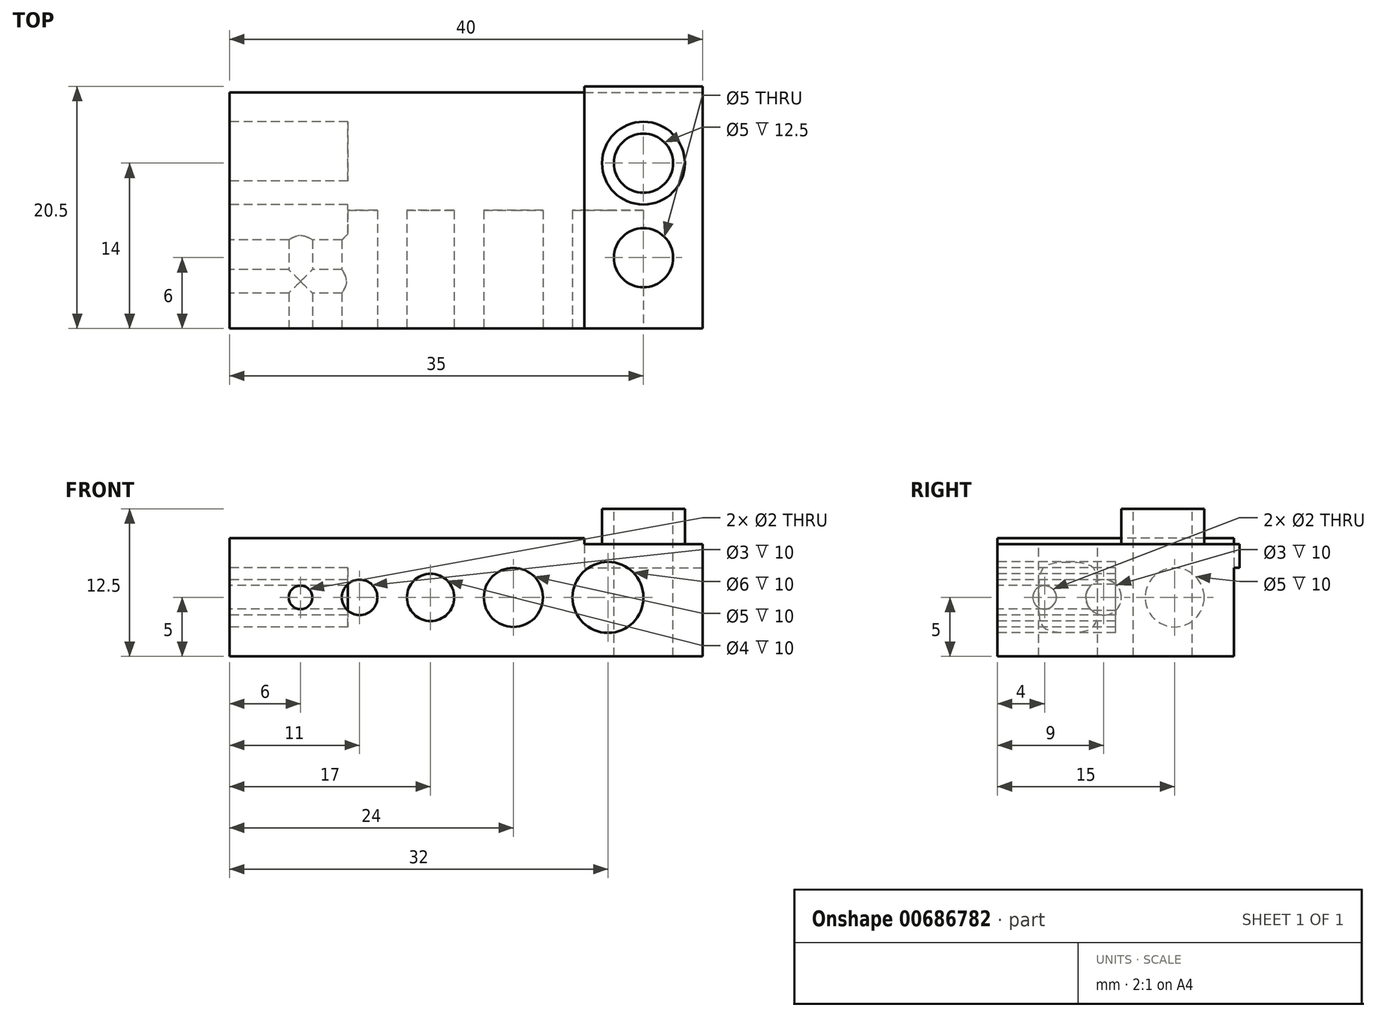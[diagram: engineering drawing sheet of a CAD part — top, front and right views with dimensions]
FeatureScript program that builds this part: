
annotation { "Feature Type Name" : "Feature", "Feature Type Description" : "" }
export const myFeature = defineFeature(function(context is Context, id is Id, definition is map)
    precondition{}
    {
        {
            var Q0;
            Q0=qCreatedBy(makeId("Top.planeOp"),FACE);
            var sketch = newSketch(context, id + "F0", { "sketchPlane" : qUnion([Q0])});
            skLineSegment(sketch, "E0.bottom", {"start": v(-20, 10) * mm, "end": v(20, 10) * mm});
            skLineSegment(sketch, "E0.top", {"start": v(-20, -10) * mm, "end": v(20, -10) * mm});
            skLineSegment(sketch, "E0.left", {"start": v(-20, 10) * mm, "end": v(-20, -10) * mm});
            skLineSegment(sketch, "E0.right", {"start": v(20, 10) * mm, "end": v(20, -10) * mm});
            skPoint(sketch, "E0.middle", {"position": v(0, 0) * mm});
            skSolve(sketch);
        }
        {
            var Q0;
            Q0=makeQuery(id+"F0.imprint","IMPRINT",FACE,{"disambiguationData":[TD([[makeQuery(id+"F0.imprint","IMPRINT",EDGE,{"derivedFrom":sQuery(id+"F0.wireOp",EDGE,"E0.bottom")}),-1.0]])]});
            extrude(context, id + "F1", {"entities" : qUnion([Q0]), "depth" : 10 * mm, "offsetDistance" : 25 * mm});
        }
        {
            var Q0;
            Q0=makeQuery(id+"F1.opExtrude","SWEPT_FACE",FACE,{"disambiguationData":[OSD([sQuery(id+"F0.wireOp",EDGE,"E0.left")])]});
            var sketch = newSketch(context, id + "F2", { "sketchPlane" : qUnion([Q0])});
            skCircle(sketch, "E1", {"center": v(6, 5) * mm, "radius": 1 * mm});
            skCircle(sketch, "E2", {"center": v(-5, 5) * mm, "radius": 2.5 * mm});
            skCircle(sketch, "E3", {"center": v(1, 5) * mm, "radius": 1.5 * mm});
            skSolve(sketch);
        }
        {
            var Q0;
            Q0 = qSketchRegion(id + "F2", true);
            extrude(context, id + "F3", {"entities" : qUnion([Q0]), "operationType" : NewBodyOperationType.REMOVE, "oppositeDirection" : true, "depth" : 10 * mm, "offsetDistance" : 25 * mm});
        }
        {
            var Q0;
            Q0=makeQuery(id+"F1.opExtrude","SWEPT_FACE",FACE,{"disambiguationData":[OSD([sQuery(id+"F0.wireOp",EDGE,"E0.top")])]});
            var sketch = newSketch(context, id + "F4", { "sketchPlane" : qUnion([Q0])});
            skCircle(sketch, "E4", {"center": v(-9, 5) * mm, "radius": 1.5 * mm});
            skCircle(sketch, "E5", {"center": v(-3, 5) * mm, "radius": 2 * mm});
            skCircle(sketch, "E6", {"center": v(4, 5) * mm, "radius": 2.5 * mm});
            skCircle(sketch, "E7", {"center": v(12, 5) * mm, "radius": 3 * mm});
            skCircle(sketch, "E8", {"center": v(-14, 5) * mm, "radius": 1 * mm});
            skSolve(sketch);
        }
        {
            var Q0;
            Q0 = qSketchRegion(id + "F4", true);
            extrude(context, id + "F5", {"entities" : qUnion([Q0]), "operationType" : NewBodyOperationType.REMOVE, "oppositeDirection" : true, "depth" : 10 * mm, "offsetDistance" : 25 * mm});
        }
        {
            var Q0;
            Q0=makeQuery(id+"F1.opExtrude","SWEPT_FACE",FACE,{"disambiguationData":[OSD([sQuery(id+"F0.wireOp",EDGE,"E0.top")])]});
            var sketch = newSketch(context, id + "F6", { "sketchPlane" : qUnion([Q0])});
            skLineSegment(sketch, "E9.bottom", {"start": v(20, 10) * mm, "end": v(10, 10) * mm});
            skLineSegment(sketch, "E9.top", {"start": v(20, 9.5) * mm, "end": v(10, 9.5) * mm});
            skLineSegment(sketch, "E9.left", {"start": v(20, 10) * mm, "end": v(20, 9.5) * mm});
            skLineSegment(sketch, "E9.right", {"start": v(10, 10) * mm, "end": v(10, 9.5) * mm});
            skSolve(sketch);
        }
        {
            var Q0;
            Q0 = qSketchRegion(id + "F6", true);
            extrude(context, id + "F7", {"entities" : qUnion([Q0]), "operationType" : NewBodyOperationType.REMOVE, "endBound" : BoundingType.THROUGH_ALL, "oppositeDirection" : true, "depth" : 25 * mm, "offsetDistance" : 25 * mm});
        }
        {
            var Q0;
            Q0=makeQuery(id+"F7.boolean.opBoolean","COPY",FACE,{"derivedFrom":makeQuery(id+"F7.opExtrude","SWEPT_FACE",FACE,{"disambiguationData":[OSD([sQuery(id+"F6.wireOp",EDGE,"E9.top")])]})});
            var sketch = newSketch(context, id + "F8", { "sketchPlane" : qUnion([Q0])});
            skCircle(sketch, "E10", {"center": v(15, 4) * mm, "radius": 2.5 * mm});
            skCircle(sketch, "E11.MirrorC", {"center": v(15, -4) * mm, "radius": 2.5 * mm});
            skSolve(sketch);
        }
        {
            var Q0;
            Q0 = qSketchRegion(id + "F8", true);
            extrude(context, id + "F9", {"entities" : qUnion([Q0]), "operationType" : NewBodyOperationType.REMOVE, "endBound" : BoundingType.THROUGH_ALL, "oppositeDirection" : true, "depth" : 25 * mm, "offsetDistance" : 25 * mm});
        }
        {
            var Q0;
            Q0=makeQuery(id+"F7.boolean.opBoolean","COPY",FACE,{"derivedFrom":makeQuery(id+"F7.opExtrude","SWEPT_FACE",FACE,{"disambiguationData":[OSD([sQuery(id+"F6.wireOp",EDGE,"E9.top")])]})});
            var sketch = newSketch(context, id + "F10", { "sketchPlane" : qUnion([Q0])});
            skCircle(sketch, "E12", {"center": v(15, 4) * mm, "radius": 3.5 * mm});
            skCircle(sketch, "E13", {"center": v(15, 4) * mm, "radius": 2.5 * mm});
            skSolve(sketch);
        }
        {
            var Q0;
            Q0 = qSketchRegion(id + "F10", true);
            extrude(context, id + "F11", {"entities" : qUnion([Q0]), "operationType" : NewBodyOperationType.ADD, "depth" : 3 * mm, "offsetDistance" : 25 * mm});
        }
        {
            var Q0;
            Q0=makeQuery(id+"F1.opExtrude","SWEPT_FACE",FACE,{"disambiguationData":[OSD([sQuery(id+"F0.wireOp",EDGE,"E0.right")])]});
            var sketch = newSketch(context, id + "F12", { "sketchPlane" : qUnion([Q0])});
            skLineSegment(sketch, "E14.bottom", {"start": v(10.5, 9.5) * mm, "end": v(10, 9.5) * mm});
            skLineSegment(sketch, "E14.top", {"start": v(10.5, 7.5) * mm, "end": v(10, 7.5) * mm});
            skLineSegment(sketch, "E14.left", {"start": v(10.5, 9.5) * mm, "end": v(10.5, 7.5) * mm});
            skLineSegment(sketch, "E14.right", {"start": v(10, 9.5) * mm, "end": v(10, 7.5) * mm});
            skSolve(sketch);
        }
        {
            var Q0;
            Q0 = qSketchRegion(id + "F12", true);
            extrude(context, id + "F13", {"entities" : qUnion([Q0]), "operationType" : NewBodyOperationType.ADD, "oppositeDirection" : true, "depth" : 10 * mm, "offsetDistance" : 25 * mm});
        }
    });
